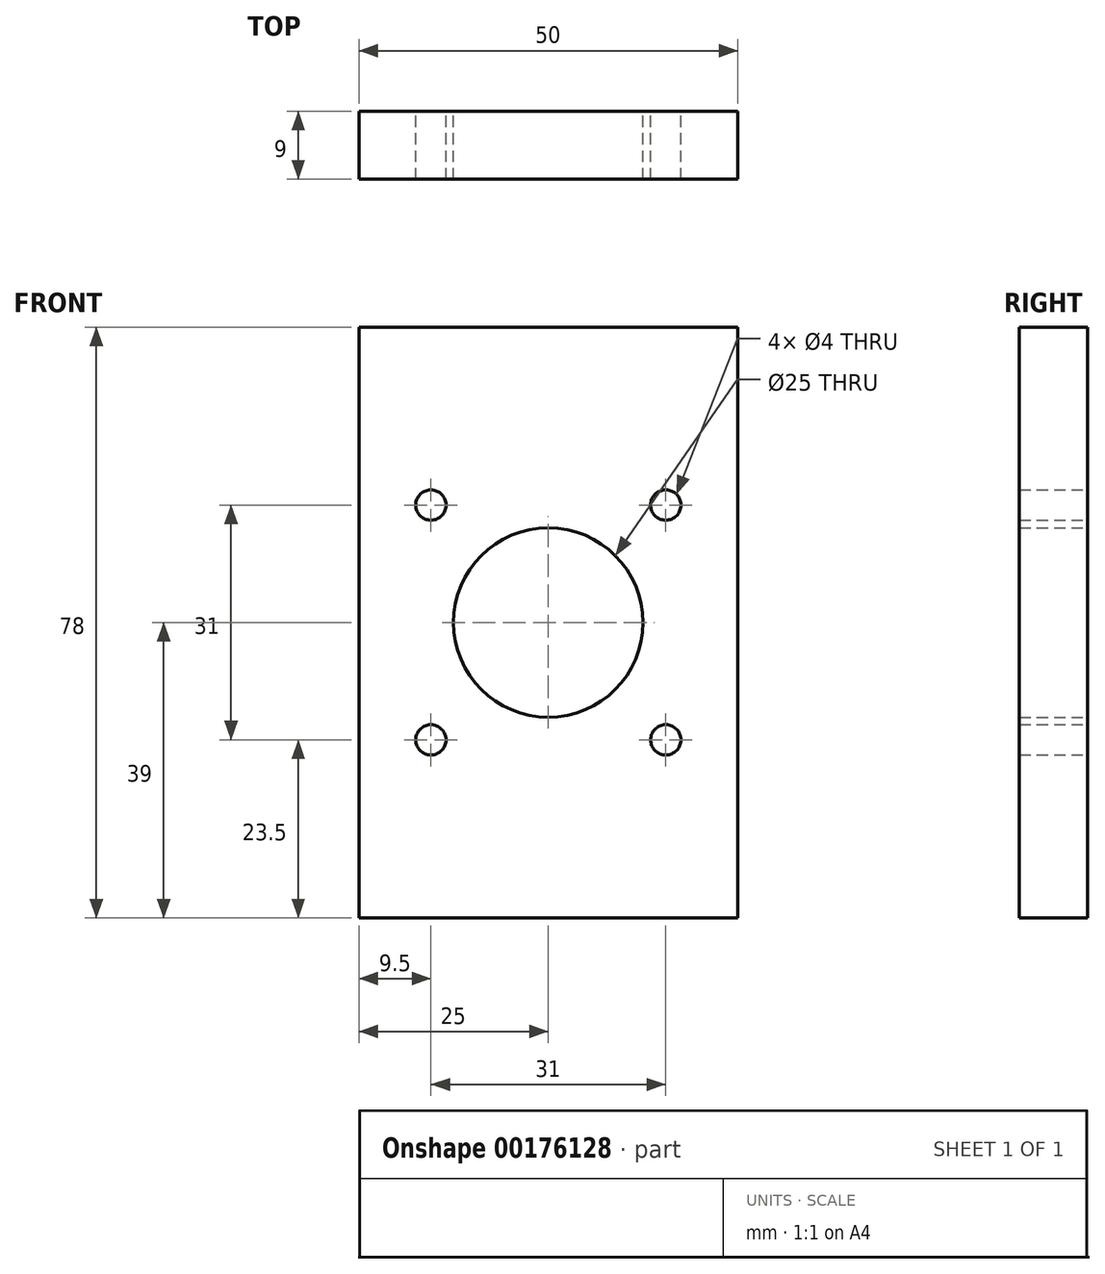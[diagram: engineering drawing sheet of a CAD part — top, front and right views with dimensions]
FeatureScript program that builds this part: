
annotation { "Feature Type Name" : "Feature", "Feature Type Description" : "" }
export const myFeature = defineFeature(function(context is Context, id is Id, definition is map)
    precondition{}
    {
        {
            var Q0;
            Q0=qCreatedBy(makeId("Front.planeOp"),FACE);
            var sketch = newSketch(context, id + "F0", { "sketchPlane" : qUnion([Q0])});
            skLineSegment(sketch, "E0.bottom", {"start": v(0, 0) * mm, "end": v(50, 0) * mm});
            skLineSegment(sketch, "E0.top", {"start": v(0, 78) * mm, "end": v(50, 78) * mm});
            skLineSegment(sketch, "E0.left", {"start": v(0, 0) * mm, "end": v(0, 78) * mm});
            skLineSegment(sketch, "E0.right", {"start": v(50, 0) * mm, "end": v(50, 78) * mm});
            skLineSegment(sketch, "E1", {"start": v(0, 78) * mm, "end": v(50, 0) * mm});
            skCircle(sketch, "E2", {"center": v(25, 39) * mm, "radius": 12.5 * mm});
            skCircle(sketch, "E3.cCircle", {"center": v(25, 39) * mm, "radius": 15.5 * mm, "construction": true});
            skPoint(sketch, "E3.cCircle.perimeterSnap0", {"position": v(25, 78) * mm});
            skLineSegment(sketch, "E3.0", {"start": v(9.5, 54.5) * mm, "end": v(40.5, 54.5) * mm});
            skLineSegment(sketch, "E3.1", {"start": v(40.5, 54.5) * mm, "end": v(40.5, 23.5) * mm});
            skLineSegment(sketch, "E3.2", {"start": v(40.5, 23.5) * mm, "end": v(9.5, 23.5) * mm});
            skLineSegment(sketch, "E3.3", {"start": v(9.5, 23.5) * mm, "end": v(9.5, 54.5) * mm});
            skPoint(sketch, "E3.0.midPoint", {"position": v(25, 54.5) * mm});
            skPoint(sketch, "E3.0.midPoint.positionSnap0", {"position": v(25, 78) * mm});
            skCircle(sketch, "E4", {"center": v(9.5, 54.5) * mm, "radius": 2 * mm});
            skCircle(sketch, "E5", {"center": v(40.5, 54.5) * mm, "radius": 2 * mm});
            skCircle(sketch, "E6", {"center": v(40.5, 23.5) * mm, "radius": 2 * mm});
            skCircle(sketch, "E7", {"center": v(9.5, 23.5) * mm, "radius": 2 * mm});
            skSolve(sketch);
        }
        {
            var Q0;
            {var subQ4=sQuery(id+"F0.wireOp",EDGE,"E0.top");Q0=makeQuery(id+"F0.imprint","IMPRINT",FACE,{"disambiguationData":[TD([[makeQuery(id+"F0.imprint","IMPRINT",EDGE,{"derivedFrom":subQ4}),-1.0]])]});}
            var Q1;
            {var subQ1=sQuery(id+"F0.wireOp",EDGE,"E0.bottom");Q1=makeQuery(id+"F0.imprint","IMPRINT",FACE,{"disambiguationData":[TD([[makeQuery(id+"F0.imprint","IMPRINT",EDGE,{"derivedFrom":subQ1}),1.0]])]});}
            var Q2;
            {var subQ0=sQuery(id+"F0.wireOp",EDGE,"E3.0");var subQ1=sQuery(id+"F0.wireOp",EDGE,"E1");var subQ2=makeQuery(id+"F0.imprint","INTERSECT",VERTEX,{"derivedFrom":[subQ1,subQ0]});Q2=makeQuery(id+"F0.imprint","IMPRINT",FACE,{"disambiguationData":[TD([[makeQuery(id+"F0.imprint","IMPRINT",EDGE,{"disambiguationData":[TD([[subQ2,-1.0]])],"derivedFrom":subQ1}),1.0]])]});}
            var Q3;
            {var subQ0=sQuery(id+"F0.wireOp",EDGE,"E3.0");var subQ1=sQuery(id+"F0.wireOp",EDGE,"E1");var subQ2=makeQuery(id+"F0.imprint","INTERSECT",VERTEX,{"derivedFrom":[subQ1,subQ0]});Q3=makeQuery(id+"F0.imprint","IMPRINT",FACE,{"disambiguationData":[TD([[makeQuery(id+"F0.imprint","IMPRINT",EDGE,{"disambiguationData":[TD([[subQ2,-1.0]])],"derivedFrom":subQ1}),-1.0]])]});}
            extrude(context, id + "F1", {"entities" : qUnion([Q0, Q1, Q2, Q3]), "depth" : 9 * mm});
        }
    });
